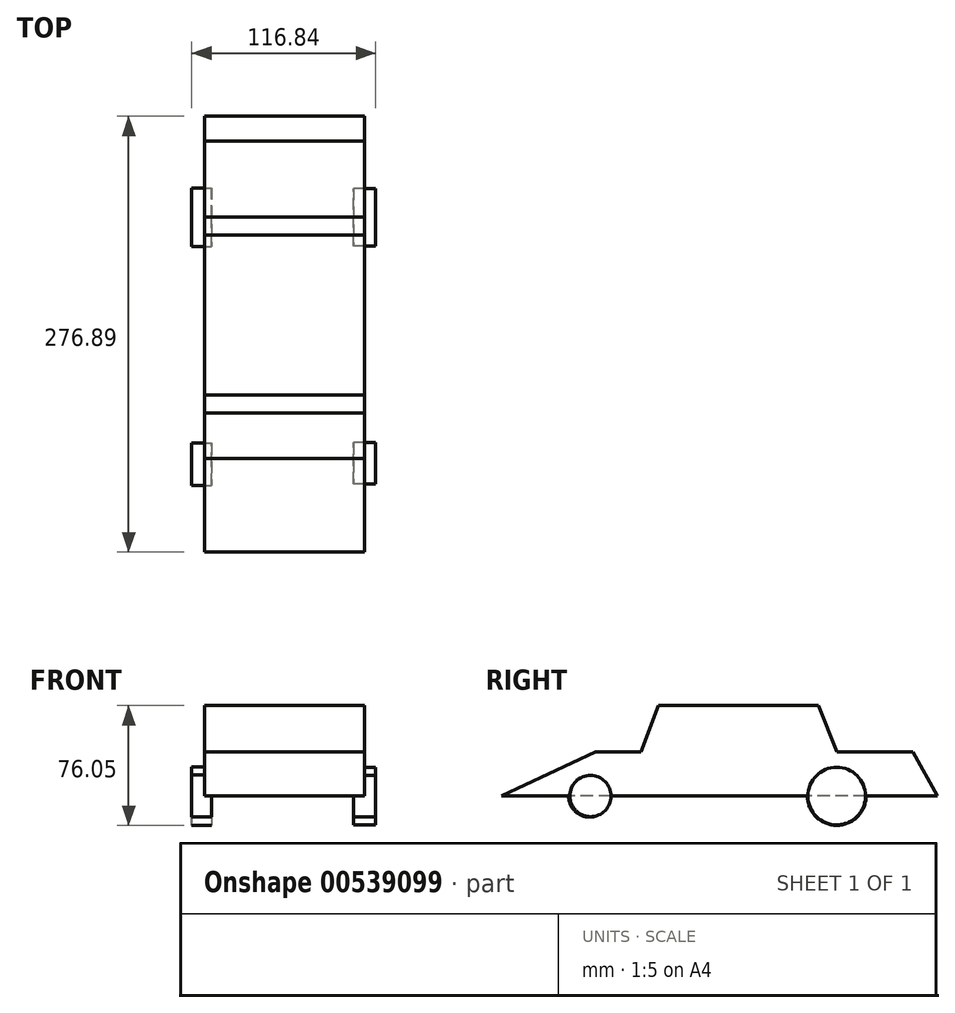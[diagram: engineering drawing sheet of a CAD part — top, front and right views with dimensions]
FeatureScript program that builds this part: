
annotation { "Feature Type Name" : "Feature", "Feature Type Description" : "" }
export const myFeature = defineFeature(function(context is Context, id is Id, definition is map)
    precondition{}
    {
        {
            var Q0;
            Q0=qCreatedBy(makeId("Right.planeOp"),FACE);
            var sketch = newSketch(context, id + "F0", { "sketchPlane" : qUnion([Q0])});
            skLineSegment(sketch, "E0", {"start": v(-50.7, 0) * mm, "end": v(150.91, 0) * mm});
            skLineSegment(sketch, "E1", {"start": v(150.91, 0) * mm, "end": v(166.67, -28.09) * mm});
            skLineSegment(sketch, "E2", {"start": v(166.67, -28.09) * mm, "end": v(-110.22, -28.09) * mm});
            skLineSegment(sketch, "E3", {"start": v(-110.22, -28.09) * mm, "end": v(-50.7, 0) * mm});
            skLineSegment(sketch, "E4", {"start": v(-21.86, 0) * mm, "end": v(-10.52, 29.3) * mm});
            skLineSegment(sketch, "E5", {"start": v(-10.52, 29.3) * mm, "end": v(91.1, 29.3) * mm});
            skLineSegment(sketch, "E6", {"start": v(91.1, 29.3) * mm, "end": v(102.63, 0) * mm});
            skLineSegment(sketch, "E7", {"start": v(150.91, 0) * mm, "end": v(102.63, 0) * mm});
            skSolve(sketch);
        }
        {
            var Q0;
            Q0 = qSketchRegion(id + "F0", true);
            extrude(context, id + "F1", {"entities" : qUnion([Q0]), "depth" : 101.6 * mm, "offsetDistance" : 25.4 * mm});
        }
        {
            var Q0;
            Q0=qCreatedBy(makeId("Right.planeOp"),FACE);
            var sketch = newSketch(context, id + "F2", { "sketchPlane" : qUnion([Q0])});
            skCircle(sketch, "E8", {"center": v(-54.4, -28.17) * mm, "radius": 13.35 * mm});
            skCircle(sketch, "E9", {"center": v(102.58, -28.17) * mm, "radius": 18.58 * mm});
            skSolve(sketch);
        }
        {
            var Q0;
            Q0 = qSketchRegion(id + "F2", true);
            extrude(context, id + "F3", {"entities" : qUnion([Q0]), "operationType" : NewBodyOperationType.ADD, "oppositeDirection" : true, "depth" : 8.13 * mm, "offsetDistance" : 25.4 * mm, "hasSecondDirection" : true, "secondDirectionOppositeDirection" : false, "secondDirectionDepth" : 4.32 * mm});
        }
        {
            var Q0;
            Q0=qCreatedBy(makeId("Right.planeOp"),FACE);
            var sketch = newSketch(context, id + "F4", { "sketchPlane" : qUnion([Q0])});
            skCircle(sketch, "E10", {"center": v(-53.82, -28.17) * mm, "radius": 13.1 * mm});
            skCircle(sketch, "E11", {"center": v(102.56, -28.17) * mm, "radius": 18.28 * mm});
            skSolve(sketch);
        }
        {
            var Q0;
            Q0 = qSketchRegion(id + "F4", true);
            extrude(context, id + "F5", {"entities" : qUnion([Q0]), "operationType" : NewBodyOperationType.ADD, "depth" : 108.7 * mm, "offsetDistance" : 25.4 * mm, "hasSecondDirection" : true, "secondDirectionOppositeDirection" : false, "secondDirectionDepth" : 94.74 * mm});
        }
    });
